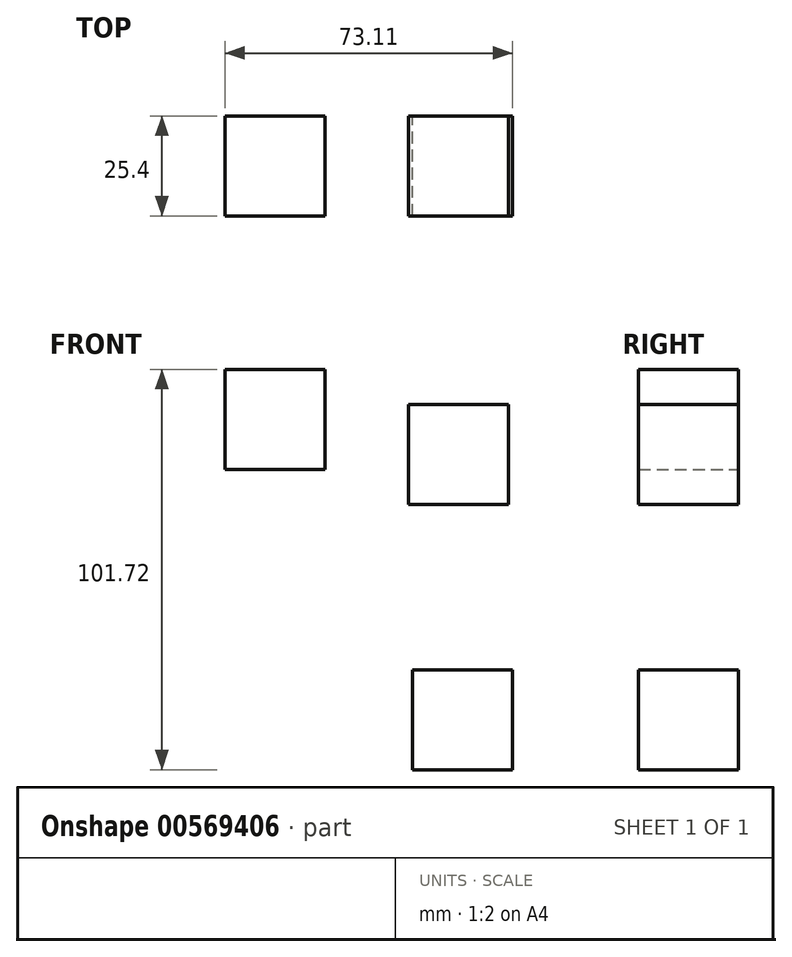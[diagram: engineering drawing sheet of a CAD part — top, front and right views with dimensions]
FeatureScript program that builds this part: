
annotation { "Feature Type Name" : "Feature", "Feature Type Description" : "" }
export const myFeature = defineFeature(function(context is Context, id is Id, definition is map)
    precondition{}
    {
        {
            var Q0;
            Q0=qCreatedBy(makeId("Front.planeOp"),FACE);
            var sketch = newSketch(context, id + "F0", { "sketchPlane" : qUnion([Q0])});
            skLineSegment(sketch, "E0.bottom", {"start": v(-40.13, 54) * mm, "end": v(-14.73, 54) * mm});
            skLineSegment(sketch, "E0.top", {"start": v(-40.13, 28.6) * mm, "end": v(-14.73, 28.6) * mm});
            skLineSegment(sketch, "E0.left", {"start": v(-40.13, 54) * mm, "end": v(-40.13, 28.6) * mm});
            skLineSegment(sketch, "E0.right", {"start": v(-14.73, 54) * mm, "end": v(-14.73, 28.6) * mm});
            skSolve(sketch);
        }
        {
            var Q0;
            Q0=makeQuery(id+"F0.imprint","IMPRINT",FACE,{"disambiguationData":[TD([[makeQuery(id+"F0.imprint","IMPRINT",EDGE,{"derivedFrom":sQuery(id+"F0.wireOp",EDGE,"E0.bottom")}),-1.0]])]});
            extrude(context, id + "F1", {"entities" : qUnion([Q0]), "depth" : 25.4 * mm, "offsetDistance" : 25.4 * mm});
        }
        {
            var Q0;
            Q0=qCreatedBy(makeId("Front.planeOp"),FACE);
            var sketch = newSketch(context, id + "F2", { "sketchPlane" : qUnion([Q0])});
            skLineSegment(sketch, "E1.bottom", {"start": v(6.58, 45.06) * mm, "end": v(31.98, 45.06) * mm});
            skLineSegment(sketch, "E1.top", {"start": v(6.58, 19.66) * mm, "end": v(31.98, 19.66) * mm});
            skLineSegment(sketch, "E1.left", {"start": v(6.58, 45.06) * mm, "end": v(6.58, 19.66) * mm});
            skLineSegment(sketch, "E1.right", {"start": v(31.98, 45.06) * mm, "end": v(31.98, 19.66) * mm});
            skSolve(sketch);
        }
        {
            var Q0;
            Q0=makeQuery(id+"F2.imprint","IMPRINT",FACE,{"disambiguationData":[TD([[makeQuery(id+"F2.imprint","IMPRINT",EDGE,{"derivedFrom":sQuery(id+"F2.wireOp",EDGE,"E1.bottom")}),-1.0]])]});
            extrude(context, id + "F3", {"entities" : qUnion([Q0]), "depth" : 25.4 * mm, "offsetDistance" : 25.4 * mm});
        }
        {
            var Q0;
            Q0=qCreatedBy(makeId("Front.planeOp"),FACE);
            var sketch = newSketch(context, id + "F4", { "sketchPlane" : qUnion([Q0])});
            skLineSegment(sketch, "E2.bottom", {"start": v(7.58, -22.32) * mm, "end": v(32.98, -22.32) * mm});
            skLineSegment(sketch, "E2.top", {"start": v(7.58, -47.72) * mm, "end": v(32.98, -47.72) * mm});
            skLineSegment(sketch, "E2.left", {"start": v(7.58, -22.32) * mm, "end": v(7.58, -47.72) * mm});
            skLineSegment(sketch, "E2.right", {"start": v(32.98, -22.32) * mm, "end": v(32.98, -47.72) * mm});
            skSolve(sketch);
        }
        {
            var Q0;
            Q0=makeQuery(id+"F4.imprint","IMPRINT",FACE,{"disambiguationData":[TD([[makeQuery(id+"F4.imprint","IMPRINT",EDGE,{"derivedFrom":sQuery(id+"F4.wireOp",EDGE,"E2.bottom")}),-1.0]])]});
            extrude(context, id + "F5", {"entities" : qUnion([Q0]), "depth" : 25.4 * mm, "offsetDistance" : 25.4 * mm});
        }
    });
